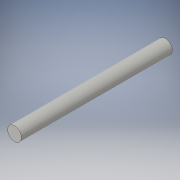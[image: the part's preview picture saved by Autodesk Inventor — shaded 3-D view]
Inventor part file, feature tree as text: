
AUTODESK INVENTOR PART (.ipt)
format: ipt  version: 2016 (Build 200138000, 138)  size: 86,528 bytes
history: native  units: in
note: dims shown in document units (in); Inventor stores cm internally (conversion verified against a paired STEP export)
features: extrude x1, sketch x1
ambient origin geometry x8: Origin, YZ Plane, XZ Plane, XY Plane, X Axis, Y Axis, Z Axis, Center Point
bodies: Solid1 (feature_tree)
feature tree (2):
  extrude  "Extrusion1"  Depth=2.75in TaperAngle=0.0deg
  sketch  "Sketch1"  dims[d0=0.25in d1=2.75in d2=0.0in]
